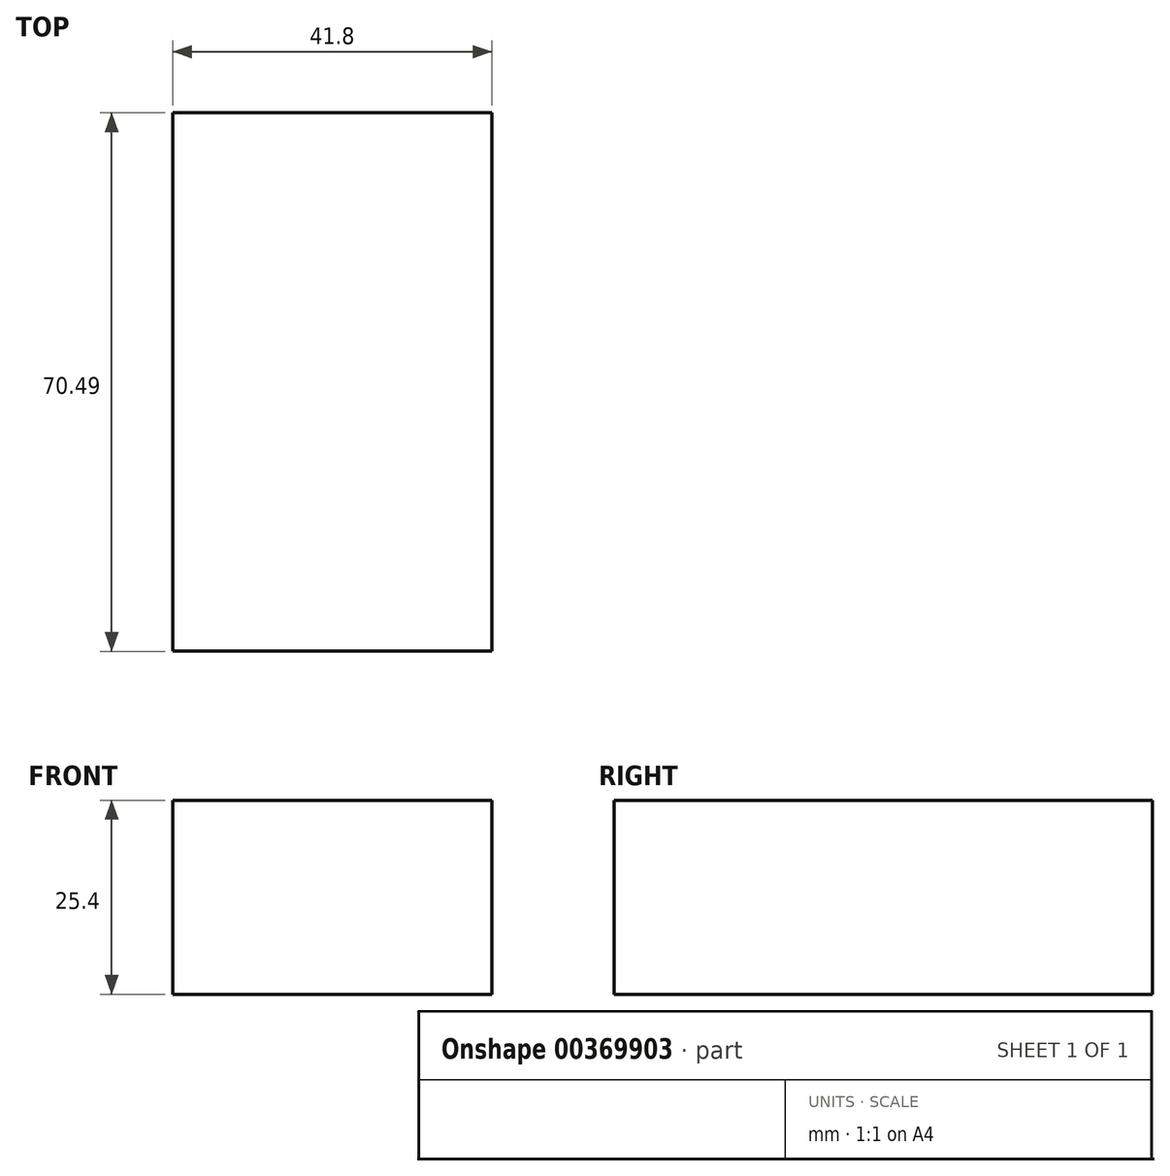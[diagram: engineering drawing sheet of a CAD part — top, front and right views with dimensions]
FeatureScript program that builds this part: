
annotation { "Feature Type Name" : "Feature", "Feature Type Description" : "" }
export const myFeature = defineFeature(function(context is Context, id is Id, definition is map)
    precondition{}
    {
        {
            var Q0;
            Q0=qCreatedBy(makeId("Top.planeOp"),FACE);
            var sketch = newSketch(context, id + "F0", { "sketchPlane" : qUnion([Q0])});
            skLineSegment(sketch, "E0.bottom", {"start": v(-12.7, 42.71) * mm, "end": v(29.1, 42.71) * mm});
            skLineSegment(sketch, "E0.top", {"start": v(-12.7, -27.78) * mm, "end": v(29.1, -27.78) * mm});
            skLineSegment(sketch, "E0.left", {"start": v(-12.7, 42.71) * mm, "end": v(-12.7, -27.78) * mm});
            skLineSegment(sketch, "E0.right", {"start": v(29.1, 42.71) * mm, "end": v(29.1, -27.78) * mm});
            skSolve(sketch);
        }
        {
            var Q0;
            Q0=makeQuery(id+"F0.imprint","IMPRINT",FACE,{"disambiguationData":[TD([[makeQuery(id+"F0.imprint","IMPRINT",EDGE,{"derivedFrom":sQuery(id+"F0.wireOp",EDGE,"E0.bottom")}),-1.0]])]});
            extrude(context, id + "F1", {"entities" : qUnion([Q0]), "depth" : 25.4 * mm});
        }
    });
